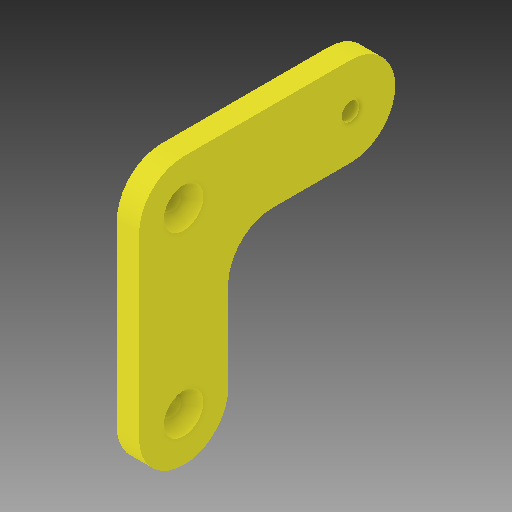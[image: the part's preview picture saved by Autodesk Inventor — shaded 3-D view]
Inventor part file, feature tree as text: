
AUTODESK INVENTOR PART (.ipt)
format: ipt  version: 2017 SP1 (Build 210196100, 196)  size: 124,416 bytes
history: native  units: in
note: dims shown in document units (in); Inventor stores cm internally (conversion verified against a paired STEP export)
features: extrude x1, chamfer x1, sketch x1
ambient origin geometry x8: Origin, YZ Plane, XZ Plane, XY Plane, X Axis, Y Axis, Z Axis, Center Point
bodies: Solid1 (feature_tree)
feature tree (3):
  extrude  "Extrusion1"  Depth=2.0in
  chamfer  "Chamfer1"  Distance=1.875in
  sketch  "Sketch1"  dims[d0=0.195in d1=2.0in d2=1.875in d3=1.0in d4=0.25in d5=0.0in d6=0.125in d7=0.125in d8=45.0deg d9=0.2in]
